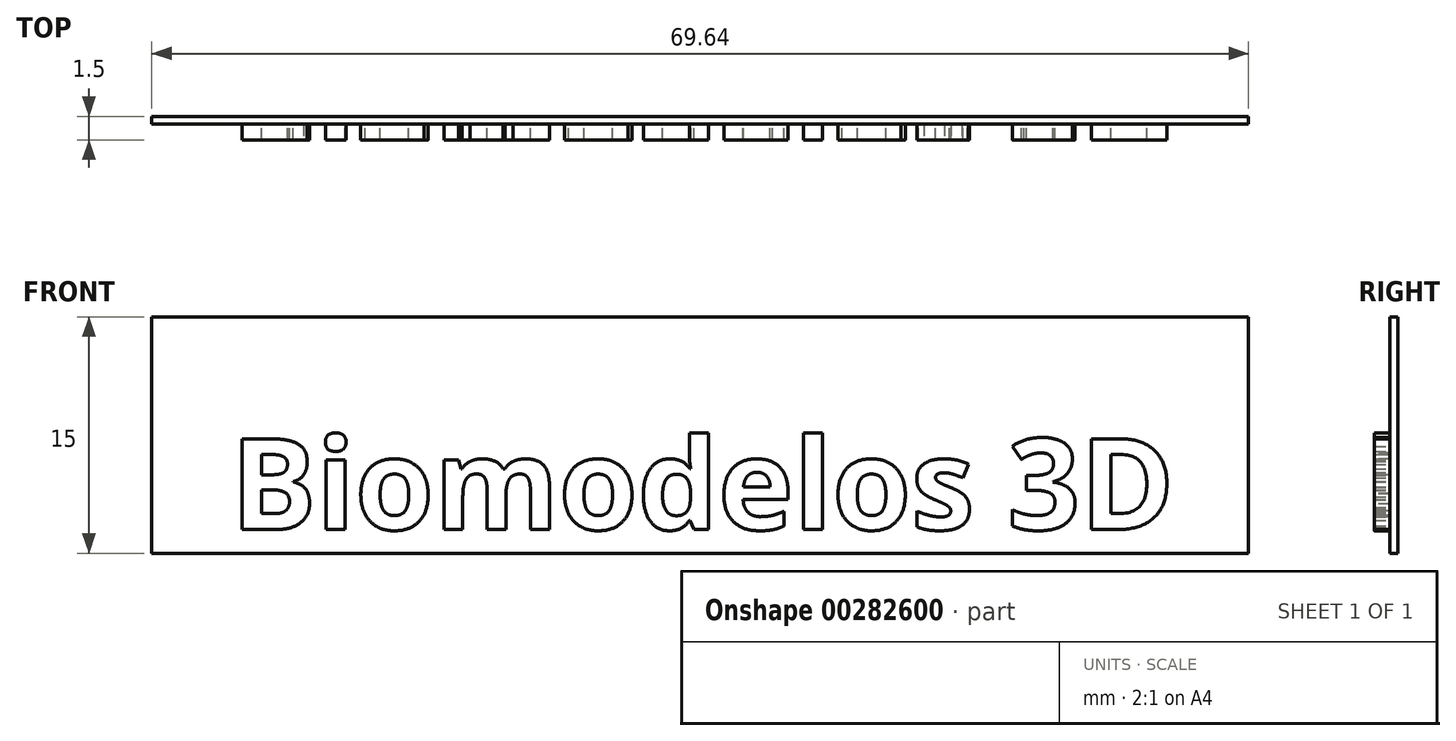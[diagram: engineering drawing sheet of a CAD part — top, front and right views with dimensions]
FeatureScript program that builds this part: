
annotation { "Feature Type Name" : "Feature", "Feature Type Description" : "" }
export const myFeature = defineFeature(function(context is Context, id is Id, definition is map)
    precondition{}
    {
        {
            var Q0;
            Q0=qCreatedBy(makeId("Front.planeOp"),FACE);
            var sketch = newSketch(context, id + "F0", { "sketchPlane" : qUnion([Q0])});
            skText(sketch, "E0", { "text": "Biomodelos 3D", "fontName": "OpenSans-Bold.ttf"});
            const initialGuessF0  = {"E0": [0, 0, 1, 0, 0.00582]};
            skSetInitialGuess(sketch, initialGuessF0);
            skSolve(sketch);
        }
        {
            var Q0;
            Q0 = qSketchRegion(id + "F0", true);
            extrude(context, id + "F1", {"entities" : qUnion([Q0]), "depth" : 1 * mm});
        }
        {
            var Q0;
            Q0=qCreatedBy(makeId("Front.planeOp"),FACE);
            var sketch = newSketch(context, id + "F2", { "sketchPlane" : qUnion([Q0])});
            skLineSegment(sketch, "E1.bottom", {"start": v(-5.01, -1.5) * mm, "end": v(64.63, -1.5) * mm});
            skLineSegment(sketch, "E1.top", {"start": v(-5.01, 13.5) * mm, "end": v(64.63, 13.5) * mm});
            skLineSegment(sketch, "E1.left", {"start": v(-5.01, -1.5) * mm, "end": v(-5.01, 13.5) * mm});
            skLineSegment(sketch, "E1.right", {"start": v(64.63, -1.5) * mm, "end": v(64.63, 13.5) * mm});
            skSolve(sketch);
        }
        {
            var Q0;
            Q0=makeQuery(id+"F2.imprint","IMPRINT",FACE,{"disambiguationData":[TD([[makeQuery(id+"F2.imprint","IMPRINT",EDGE,{"derivedFrom":sQuery(id+"F2.wireOp",EDGE,"E1.bottom")}),1.0]])]});
            extrude(context, id + "F3", {"entities" : qUnion([Q0]), "operationType" : NewBodyOperationType.ADD, "oppositeDirection" : true, "depth" : 0.5 * mm});
        }
    });
